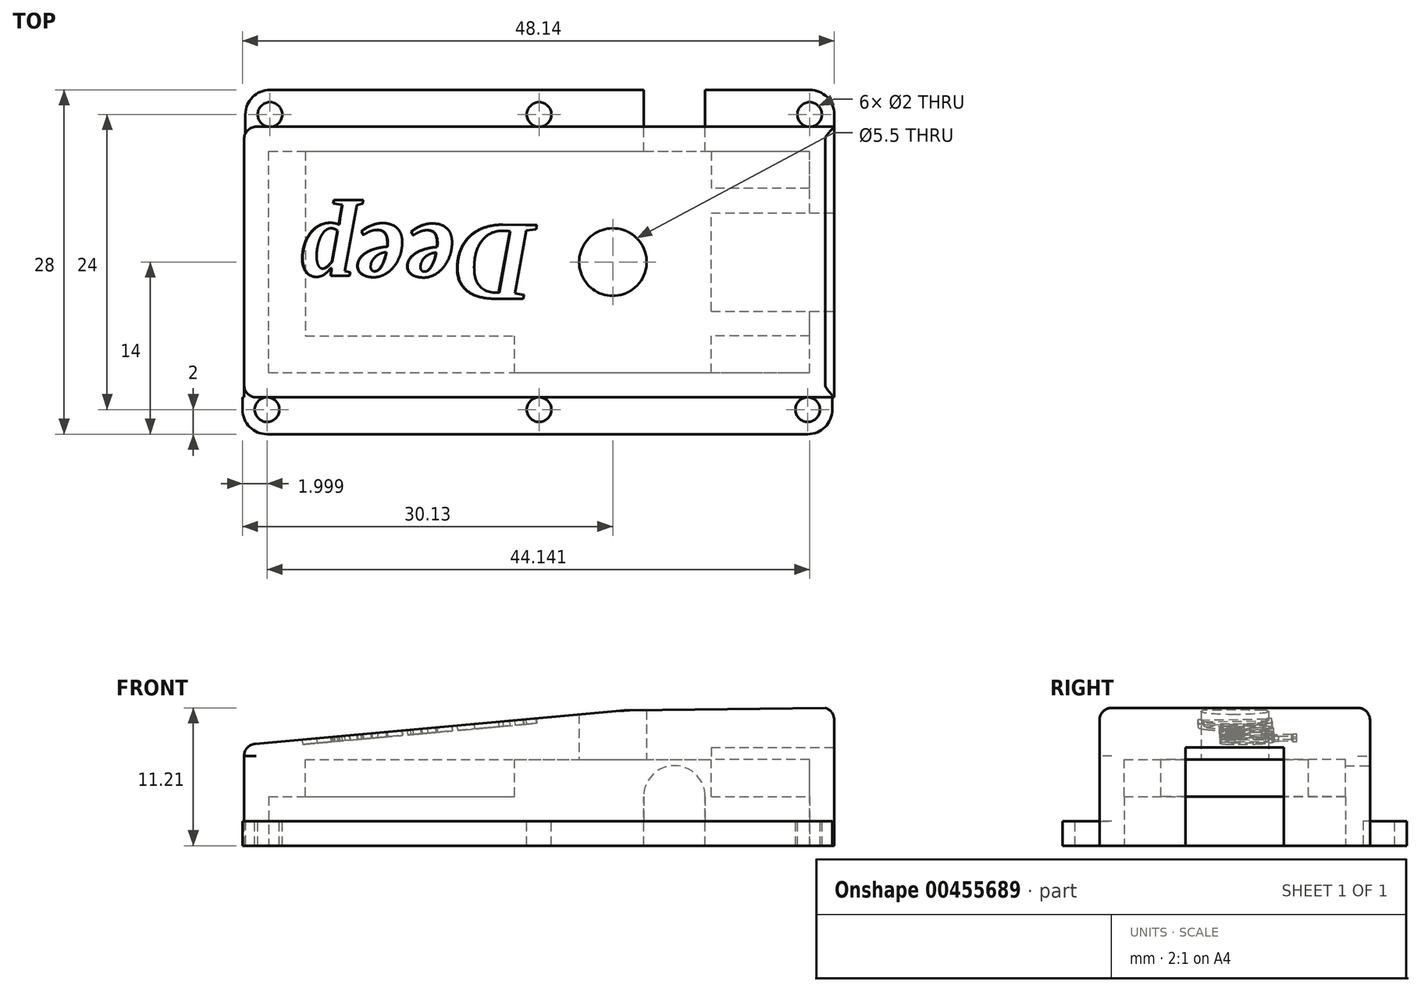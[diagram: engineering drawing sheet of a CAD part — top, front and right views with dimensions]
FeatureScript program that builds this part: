
annotation { "Feature Type Name" : "Feature", "Feature Type Description" : "" }
export const myFeature = defineFeature(function(context is Context, id is Id, definition is map)
    precondition{}
    {
        {
            var Q0;
            Q0=qCreatedBy(makeId("Front.planeOp"),FACE);
            var sketch = newSketch(context, id + "F0", { "sketchPlane" : qUnion([Q0])});
            skLineSegment(sketch, "E0", {"start": v(-24, 0) * mm, "end": v(-24, 7.34) * mm});
            skLineSegment(sketch, "E1", {"start": v(24, 0) * mm, "end": v(24, 10.25) * mm});
            skLineSegment(sketch, "E2", {"start": v(-24, 0) * mm, "end": v(24, 0) * mm});
            skPoint(sketch, "E3", {"position": v(7, 11) * mm});
            skPoint(sketch, "E4.visualSharp", {"position": v(-24, 8) * mm});
            skArc(sketch, "E4.filletArc", {"start": v(-23.4, 8.26) * mm, "mid": v(-23.83, 7.9) * mm, "end": v(-24, 7.34) * mm});
            skPoint(sketch, "E5.visualSharp", {"position": v(24, 9) * mm});
            skArc(sketch, "E5.filletArc", {"start": v(24, 10.25) * mm, "mid": v(23.8, 10.85) * mm, "end": v(23.27, 11.21) * mm});
            skLineSegment(sketch, "E6", {"start": v(-23.4, 8.26) * mm, "end": v(6.62, 10.97) * mm});
            skLineSegment(sketch, "E7", {"start": v(23.27, 11.21) * mm, "end": v(7.38, 11) * mm});
            skArc(sketch, "E8.filletArc", {"start": v(7.38, 11) * mm, "mid": v(7, 11) * mm, "end": v(6.62, 10.97) * mm});
            skSolve(sketch);
        }
        {
            var Q0;
            Q0=makeQuery(id+"F0.imprint","IMPRINT",FACE,{"disambiguationData":[TD([[makeQuery(id+"F0.imprint","IMPRINT",EDGE,{"derivedFrom":sQuery(id+"F0.wireOp",EDGE,"E0")}),-1.0]])]});
            extrude(context, id + "F1", {"entities" : qUnion([Q0]), "depth" : 22 * mm});
        }
        {
            var Q0;
            Q0=makeQuery(id+"F1.opExtrude","SWEPT_FACE",FACE,{"disambiguationData":[OSD([sQuery(id+"F0.wireOp",EDGE,"E2")])]});
            var sketch = newSketch(context, id + "F2", { "sketchPlane" : qUnion([Q0])});
            skLineSegment(sketch, "E9.bottom", {"start": v(-22, 20) * mm, "end": v(22, 20) * mm});
            skLineSegment(sketch, "E9.top", {"start": v(-22, 2) * mm, "end": v(22, 2) * mm});
            skLineSegment(sketch, "E9.left", {"start": v(-22, 20) * mm, "end": v(-22, 2) * mm});
            skLineSegment(sketch, "E9.right", {"start": v(22, 20) * mm, "end": v(22, 2) * mm});
            skSolve(sketch);
        }
        {
            var Q0;
            Q0=makeQuery(id+"F2.imprint","IMPRINT",FACE,{"disambiguationData":[TD([[makeQuery(id+"F2.imprint","IMPRINT",EDGE,{"derivedFrom":sQuery(id+"F2.wireOp",EDGE,"E9.bottom")}),-1.0]])]});
            extrude(context, id + "F3", {"entities" : qUnion([Q0]), "operationType" : NewBodyOperationType.REMOVE, "depth" : -7 * mm});
        }
        {
            var Q0;
            Q0=makeQuery(id+"F3.boolean.opBoolean","COPY",FACE,{"derivedFrom":makeQuery(id+"F3.opExtrude","CAP_FACE",FACE,{"disambiguationData":[OSD([sQuery(id+"F2.wireOp",EDGE,"E9.bottom"),sQuery(id+"F2.wireOp",EDGE,"E9.top"),sQuery(id+"F2.wireOp",EDGE,"E9.left"),sQuery(id+"F2.wireOp",EDGE,"E9.right")])],"isStart":false})});
            var sketch = newSketch(context, id + "F4", { "sketchPlane" : qUnion([Q0])});
            skLineSegment(sketch, "E10.bottom", {"start": v(14, 15) * mm, "end": v(22, 15) * mm});
            skLineSegment(sketch, "E10.top", {"start": v(14, 7) * mm, "end": v(22, 7) * mm});
            skLineSegment(sketch, "E10.left", {"start": v(14, 15) * mm, "end": v(14, 7) * mm});
            skLineSegment(sketch, "E10.right", {"start": v(22, 15) * mm, "end": v(22, 7) * mm});
            skSolve(sketch);
        }
        {
            var Q0;
            Q0=makeQuery(id+"F4.imprint","IMPRINT",FACE,{"disambiguationData":[TD([[makeQuery(id+"F4.imprint","IMPRINT",EDGE,{"derivedFrom":sQuery(id+"F4.wireOp",EDGE,"E10.bottom")}),-1.0]])]});
            extrude(context, id + "F5", {"entities" : qUnion([Q0]), "operationType" : NewBodyOperationType.REMOVE, "depth" : -1 * mm});
        }
        {
            var Q0;
            Q0=makeQuery(id+"F1.opExtrude","SWEPT_FACE",FACE,{"disambiguationData":[OSD([sQuery(id+"F0.wireOp",EDGE,"E1")])]});
            var sketch = newSketch(context, id + "F6", { "sketchPlane" : qUnion([Q0])});
            skLineSegment(sketch, "E11.bottom", {"start": v(-15, 0) * mm, "end": v(-7, 0) * mm});
            skLineSegment(sketch, "E11.top", {"start": v(-15, 8) * mm, "end": v(-7, 8) * mm});
            skLineSegment(sketch, "E11.left", {"start": v(-15, 0) * mm, "end": v(-15, 8) * mm});
            skLineSegment(sketch, "E11.right", {"start": v(-7, 0) * mm, "end": v(-7, 8) * mm});
            skSolve(sketch);
        }
        {
            var Q0;
            {var subQ0=sQuery(id+"F6.wireOp",EDGE,"E11.bottom");Q0=makeQuery(id+"F6.imprint","IMPRINT",FACE,{"disambiguationData":[TD([[makeQuery(id+"F6.imprint","IMPRINT",EDGE,{"derivedFrom":subQ0}),1.0]])]});}
            var Q1;
            {var subQ0=sQuery(id+"F6.wireOp",EDGE,"E11.top");Q1=makeQuery(id+"F6.imprint","IMPRINT",FACE,{"disambiguationData":[TD([[makeQuery(id+"F6.imprint","IMPRINT",EDGE,{"derivedFrom":subQ0}),-1.0]])]});}
            extrude(context, id + "F7", {"entities" : qUnion([Q0, Q1]), "operationType" : NewBodyOperationType.REMOVE, "oppositeDirection" : true, "depth" : 2 * mm});
        }
        {
            var Q0;
            Q0=makeQuery(id+"F3.boolean.opBoolean","COPY",FACE,{"derivedFrom":makeQuery(id+"F3.opExtrude","CAP_FACE",FACE,{"disambiguationData":[OSD([sQuery(id+"F2.wireOp",EDGE,"E9.bottom"),sQuery(id+"F2.wireOp",EDGE,"E9.top"),sQuery(id+"F2.wireOp",EDGE,"E9.left"),sQuery(id+"F2.wireOp",EDGE,"E9.right")])],"isStart":false})});
            var sketch = newSketch(context, id + "F8", { "sketchPlane" : qUnion([Q0])});
            skCircle(sketch, "E12", {"center": v(6, 11) * mm, "radius": 2.75 * mm});
            skSolve(sketch);
        }
        {
            var Q0;
            Q0=makeQuery(id+"F8.imprint","IMPRINT",FACE,{"disambiguationData":[TD([[makeQuery(id+"F8.imprint","IMPRINT",EDGE,{"derivedFrom":sQuery(id+"F8.wireOp",EDGE,"E12")}),1.0]])]});
            extrude(context, id + "F9", {"entities" : qUnion([Q0]), "operationType" : NewBodyOperationType.REMOVE, "oppositeDirection" : true, "depth" : 10 * mm});
        }
        {
            var Q0;
            Q0=makeQuery(id+"F3.boolean.opBoolean","COPY",FACE,{"derivedFrom":makeQuery(id+"F3.opExtrude","CAP_FACE",FACE,{"disambiguationData":[OSD([sQuery(id+"F2.wireOp",EDGE,"E9.bottom"),sQuery(id+"F2.wireOp",EDGE,"E9.top"),sQuery(id+"F2.wireOp",EDGE,"E9.left"),sQuery(id+"F2.wireOp",EDGE,"E9.right")])],"isStart":false})});
            var sketch = newSketch(context, id + "F10", { "sketchPlane" : qUnion([Q0])});
            skLineSegment(sketch, "E13.bottom", {"start": v(22, 2) * mm, "end": v(14, 2) * mm});
            skLineSegment(sketch, "E13.top", {"start": v(22, 5) * mm, "end": v(14, 5) * mm});
            skLineSegment(sketch, "E13.left", {"start": v(22, 2) * mm, "end": v(22, 5) * mm});
            skLineSegment(sketch, "E13.right", {"start": v(14, 2) * mm, "end": v(14, 5) * mm});
            skLineSegment(sketch, "E14.bottom", {"start": v(22, 20) * mm, "end": v(14, 20) * mm});
            skLineSegment(sketch, "E14.top", {"start": v(22, 17) * mm, "end": v(14, 17) * mm});
            skLineSegment(sketch, "E14.left", {"start": v(22, 20) * mm, "end": v(22, 17) * mm});
            skLineSegment(sketch, "E14.right", {"start": v(14, 20) * mm, "end": v(14, 17) * mm});
            skLineSegment(sketch, "E15.bottom", {"start": v(-22, 20) * mm, "end": v(-2, 20) * mm});
            skLineSegment(sketch, "E15.top", {"start": v(-22, 17) * mm, "end": v(-2, 17) * mm});
            skLineSegment(sketch, "E15.left", {"start": v(-22, 20) * mm, "end": v(-22, 17) * mm});
            skLineSegment(sketch, "E15.right", {"start": v(-2, 20) * mm, "end": v(-2, 17) * mm});
            skLineSegment(sketch, "E16.bottom", {"start": v(-22, 2) * mm, "end": v(-19, 2) * mm});
            skLineSegment(sketch, "E16.top", {"start": v(-22, 5) * mm, "end": v(-19, 5) * mm});
            skLineSegment(sketch, "E16.left", {"start": v(-22, 2) * mm, "end": v(-22, 5) * mm});
            skLineSegment(sketch, "E16.right", {"start": v(-19, 2) * mm, "end": v(-19, 5) * mm});
            skSolve(sketch);
        }
        {
            var Q0;
            Q0=makeQuery(id+"F10.imprint","IMPRINT",FACE,{"disambiguationData":[TD([[makeQuery(id+"F10.imprint","IMPRINT",EDGE,{"derivedFrom":sQuery(id+"F10.wireOp",EDGE,"E15.bottom")}),-1.0]])]});
            var Q1;
            Q1=makeQuery(id+"F10.imprint","IMPRINT",FACE,{"disambiguationData":[TD([[makeQuery(id+"F10.imprint","IMPRINT",EDGE,{"derivedFrom":sQuery(id+"F10.wireOp",EDGE,"E16.bottom")}),1.0]])]});
            var Q2;
            Q2=makeQuery(id+"F10.imprint","IMPRINT",FACE,{"disambiguationData":[TD([[makeQuery(id+"F10.imprint","IMPRINT",EDGE,{"derivedFrom":sQuery(id+"F10.wireOp",EDGE,"E13.bottom")}),1.0]])]});
            var Q3;
            Q3=makeQuery(id+"F10.imprint","IMPRINT",FACE,{"disambiguationData":[TD([[makeQuery(id+"F10.imprint","IMPRINT",EDGE,{"derivedFrom":sQuery(id+"F10.wireOp",EDGE,"E14.bottom")}),-1.0]])]});
            extrude(context, id + "F11", {"entities" : qUnion([Q0, Q1, Q2, Q3]), "operationType" : NewBodyOperationType.ADD, "depth" : 3 * mm});
        }
        {
            var Q0;
            Q0=makeQuery(id+"F1.opExtrude","CAP_FACE",FACE,{"disambiguationData":[OSD([sQuery(id+"F0.wireOp",EDGE,"E0"),sQuery(id+"F0.wireOp",EDGE,"E1"),sQuery(id+"F0.wireOp",EDGE,"E2"),sQuery(id+"F0.wireOp",EDGE,"Oknbtmik-333Q-qwfd-Srco-IpxuO3KOyoef"),sQuery(id+"F0.wireOp",EDGE,"E4.filletArc"),sQuery(id+"F0.wireOp",EDGE,"E5.filletArc")])],"isStart":true});
            var sketch = newSketch(context, id + "F12", { "sketchPlane" : qUnion([Q0])});
            skLineSegment(sketch, "E17.bottom", {"start": v(-24.01, 2) * mm, "end": v(23.9, 2) * mm});
            skLineSegment(sketch, "E17.top", {"start": v(-24.01, 0) * mm, "end": v(23.9, 0) * mm});
            skLineSegment(sketch, "E17.left", {"start": v(-24.01, 2) * mm, "end": v(-24.01, 0) * mm});
            skLineSegment(sketch, "E17.right", {"start": v(23.9, 2) * mm, "end": v(23.9, 0) * mm});
            skSolve(sketch);
        }
        {
            var Q0;
            Q0=makeQuery(id+"F12.imprint","IMPRINT",FACE,{"disambiguationData":[TD([[makeQuery(id+"F12.imprint","IMPRINT",EDGE,{"derivedFrom":sQuery(id+"F12.wireOp",EDGE,"E17.bottom")}),-1.0]])]});
            extrude(context, id + "F13", {"entities" : qUnion([Q0]), "operationType" : NewBodyOperationType.ADD, "depth" : 3 * mm});
        }
        {
            var Q0;
            Q0=makeQuery(id+"F1.opExtrude","CAP_FACE",FACE,{"disambiguationData":[OSD([sQuery(id+"F0.wireOp",EDGE,"E0"),sQuery(id+"F0.wireOp",EDGE,"E1"),sQuery(id+"F0.wireOp",EDGE,"E2"),sQuery(id+"F0.wireOp",EDGE,"Oknbtmik-333Q-qwfd-Srco-IpxuO3KOyoef"),sQuery(id+"F0.wireOp",EDGE,"E4.filletArc"),sQuery(id+"F0.wireOp",EDGE,"E5.filletArc")])],"isStart":false});
            var sketch = newSketch(context, id + "F14", { "sketchPlane" : qUnion([Q0])});
            skLineSegment(sketch, "E18.bottom", {"start": v(-24.13, 2) * mm, "end": v(23.85, 2) * mm});
            skLineSegment(sketch, "E18.top", {"start": v(-24.13, 0) * mm, "end": v(23.85, 0) * mm});
            skLineSegment(sketch, "E18.left", {"start": v(-24.13, 2) * mm, "end": v(-24.13, 0) * mm});
            skLineSegment(sketch, "E18.right", {"start": v(23.85, 2) * mm, "end": v(23.85, 0) * mm});
            skSolve(sketch);
        }
        {
            var Q0;
            Q0=makeQuery(id+"F14.imprint","IMPRINT",FACE,{"disambiguationData":[TD([[makeQuery(id+"F14.imprint","IMPRINT",EDGE,{"derivedFrom":sQuery(id+"F14.wireOp",EDGE,"E18.bottom")}),-1.0]])]});
            extrude(context, id + "F15", {"entities" : qUnion([Q0]), "operationType" : NewBodyOperationType.ADD, "depth" : 3 * mm});
        }
        {
            var Q0;
            Q0=makeQuery(id+"F13.opExtrude","CAP_EDGE",EDGE,{"disambiguationData":[OSD([sQuery(id+"F12.wireOp",EDGE,"E17.right")])],"isStart":false});
            fillet(context, id + "F16", {"entities" : qUnion([Q0]), "radius" : 2 * mm, "tangentPropagation" : true, "allowEdgeOverflow" : false});
        }
        {
            var Q0;
            Q0=makeQuery(id+"F13.opExtrude","CAP_EDGE",EDGE,{"disambiguationData":[OSD([sQuery(id+"F12.wireOp",EDGE,"E17.left")])],"isStart":false});
            var Q1;
            Q1=makeQuery(id+"F15.opExtrude","CAP_EDGE",EDGE,{"disambiguationData":[OSD([sQuery(id+"F14.wireOp",EDGE,"E18.right")])],"isStart":false});
            var Q2;
            Q2=makeQuery(id+"F15.opExtrude","CAP_EDGE",EDGE,{"disambiguationData":[OSD([sQuery(id+"F14.wireOp",EDGE,"E18.left")])],"isStart":false});
            fillet(context, id + "F17", {"entities" : qUnion([Q0, Q1, Q2]), "radius" : 2 * mm, "tangentPropagation" : true, "allowEdgeOverflow" : false});
        }
        {
            var Q0;
            Q0=makeQuery(id+"F13.opExtrude","SWEPT_FACE",FACE,{"disambiguationData":[OSD([sQuery(id+"F12.wireOp",EDGE,"E17.bottom")])]});
            var sketch = newSketch(context, id + "F18", { "sketchPlane" : qUnion([Q0])});
            skCircle(sketch, "E19", {"center": v(0, 1) * mm, "radius": 1 * mm});
            skCircle(sketch, "E20", {"center": v(22.01, 1) * mm, "radius": 1 * mm});
            skCircle(sketch, "E21", {"center": v(-21.9, 1) * mm, "radius": 1 * mm});
            skCircle(sketch, "E22", {"center": v(0, -23) * mm, "radius": 1 * mm});
            skCircle(sketch, "E23", {"center": v(-22.13, -23) * mm, "radius": 1 * mm});
            skCircle(sketch, "E24", {"center": v(21.85, -23) * mm, "radius": 1 * mm});
            skSolve(sketch);
        }
        {
            var Q0;
            Q0=makeQuery(id+"F18.imprint","IMPRINT",FACE,{"disambiguationData":[TD([[makeQuery(id+"F18.imprint","IMPRINT",EDGE,{"derivedFrom":sQuery(id+"F18.wireOp",EDGE,"E21")}),1.0]])]});
            var Q1;
            Q1=makeQuery(id+"F18.imprint","IMPRINT",FACE,{"disambiguationData":[TD([[makeQuery(id+"F18.imprint","IMPRINT",EDGE,{"derivedFrom":sQuery(id+"F18.wireOp",EDGE,"E19")}),1.0]])]});
            var Q2;
            Q2=makeQuery(id+"F18.imprint","IMPRINT",FACE,{"disambiguationData":[TD([[makeQuery(id+"F18.imprint","IMPRINT",EDGE,{"derivedFrom":sQuery(id+"F18.wireOp",EDGE,"E20")}),1.0]])]});
            var Q3;
            Q3=makeQuery(id+"F18.imprint","IMPRINT",FACE,{"disambiguationData":[TD([[makeQuery(id+"F18.imprint","IMPRINT",EDGE,{"derivedFrom":sQuery(id+"F18.wireOp",EDGE,"E23")}),1.0]])]});
            var Q4;
            Q4=makeQuery(id+"F18.imprint","IMPRINT",FACE,{"disambiguationData":[TD([[makeQuery(id+"F18.imprint","IMPRINT",EDGE,{"derivedFrom":sQuery(id+"F18.wireOp",EDGE,"E22")}),1.0]])]});
            var Q5;
            Q5=makeQuery(id+"F18.imprint","IMPRINT",FACE,{"disambiguationData":[TD([[makeQuery(id+"F18.imprint","IMPRINT",EDGE,{"derivedFrom":sQuery(id+"F18.wireOp",EDGE,"E24")}),1.0]])]});
            extrude(context, id + "F19", {"entities" : qUnion([Q0, Q1, Q2, Q3, Q4, Q5]), "operationType" : NewBodyOperationType.REMOVE, "oppositeDirection" : true, "depth" : 2 * mm});
        }
        {
            var Q0;
            {var subQ0=sQuery(id+"F0.wireOp",EDGE,"E0");Q0=makeQuery(id+"F15.boolean.opBoolean","SPLIT",EDGE,{"disambiguationData":[topologyDisambiguationEdgeConnected([makeQuery(id+"F1.opExtrude","CAP_FACE",FACE,{"disambiguationData":[OSD([subQ0,sQuery(id+"F0.wireOp",EDGE,"E1"),sQuery(id+"F0.wireOp",EDGE,"E2"),sQuery(id+"F0.wireOp",EDGE,"E4.filletArc"),sQuery(id+"F0.wireOp",EDGE,"6WC63ifF-hcEu-kARe-1SZb-fn5sgA7jzdy6")])],"isStart":false})])],"derivedFrom":makeQuery(id+"F1.opExtrude","CAP_EDGE",EDGE,{"disambiguationData":[OSD([subQ0])],"isStart":false})});}
            fillet(context, id + "F20", {"entities" : qUnion([Q0]), "radius" : 1 * mm, "tangentPropagation" : true, "allowEdgeOverflow" : false});
        }
        {
            var Q0;
            Q0=makeQuery(id+"F1.opExtrude","CAP_EDGE",EDGE,{"disambiguationData":[OSD([sQuery(id+"F0.wireOp",EDGE,"E0")])],"isStart":true});
            fillet(context, id + "F21", {"entities" : qUnion([Q0]), "radius" : 1 * mm, "tangentPropagation" : true, "allowEdgeOverflow" : false});
        }
        {
            var Q0;
            Q0=makeQuery(id+"F13.opExtrude","CAP_FACE",FACE,{"disambiguationData":[OSD([sQuery(id+"F12.wireOp",EDGE,"E17.bottom"),sQuery(id+"F12.wireOp",EDGE,"E17.top"),sQuery(id+"F12.wireOp",EDGE,"E17.left"),sQuery(id+"F12.wireOp",EDGE,"E17.right")])],"isStart":false});
            var sketch = newSketch(context, id + "F22", { "sketchPlane" : qUnion([Q0])});
            skLineSegment(sketch, "E25.bottom", {"start": v(-13.51, 0) * mm, "end": v(-8.51, 0) * mm});
            skLineSegment(sketch, "E25.top", {"start": v(-11.01, 6.5) * mm, "end": v(-11.01, 6.5) * mm});
            skLineSegment(sketch, "E25.left", {"start": v(-13.51, 0) * mm, "end": v(-13.51, 4) * mm});
            skLineSegment(sketch, "E25.right", {"start": v(-8.51, 0) * mm, "end": v(-8.51, 4) * mm});
            skPoint(sketch, "E26.visualSharp", {"position": v(-13.51, 6.5) * mm});
            skArc(sketch, "E26.filletArc", {"start": v(-11.01, 6.5) * mm, "mid": v(-12.78, 5.77) * mm, "end": v(-13.51, 4) * mm});
            skPoint(sketch, "E27.visualSharp", {"position": v(-8.51, 6.5) * mm});
            skArc(sketch, "E27.filletArc", {"start": v(-8.51, 4) * mm, "mid": v(-9.24, 5.77) * mm, "end": v(-11.01, 6.5) * mm});
            skSolve(sketch);
        }
        {
            var Q0;
            {var subQ0=sQuery(id+"F22.wireOp",EDGE,"E25.bottom");Q0=makeQuery(id+"F22.imprint","IMPRINT",FACE,{"disambiguationData":[TD([[makeQuery(id+"F22.imprint","IMPRINT",EDGE,{"derivedFrom":subQ0}),1.0]])]});}
            var Q1;
            {var subQ1=sQuery(id+"F22.wireOp",EDGE,"E26.filletArc");Q1=makeQuery(id+"F22.imprint","IMPRINT",FACE,{"disambiguationData":[TD([[makeQuery(id+"F22.imprint","IMPRINT",EDGE,{"derivedFrom":subQ1}),1.0]])]});}
            extrude(context, id + "F23", {"entities" : qUnion([Q0, Q1]), "operationType" : NewBodyOperationType.REMOVE, "oppositeDirection" : true, "depth" : 6 * mm});
        }
        {
            var Q0;
            Q0=makeQuery(id+"F3.boolean.opBoolean","COPY",FACE,{"derivedFrom":makeQuery(id+"F3.opExtrude","CAP_FACE",FACE,{"disambiguationData":[OSD([sQuery(id+"F2.wireOp",EDGE,"E9.bottom"),sQuery(id+"F2.wireOp",EDGE,"E9.top"),sQuery(id+"F2.wireOp",EDGE,"E9.left"),sQuery(id+"F2.wireOp",EDGE,"E9.right")])],"isStart":false})});
            var sketch = newSketch(context, id + "F24", { "sketchPlane" : qUnion([Q0])});
            skLineSegment(sketch, "E28.bottom", {"start": v(-22, 17) * mm, "end": v(-19, 17) * mm});
            skLineSegment(sketch, "E28.top", {"start": v(-22, 5) * mm, "end": v(-19, 5) * mm});
            skLineSegment(sketch, "E28.left", {"start": v(-22, 17) * mm, "end": v(-22, 5) * mm});
            skLineSegment(sketch, "E28.right", {"start": v(-19, 17) * mm, "end": v(-19, 5) * mm});
            skSolve(sketch);
        }
        {
            var Q0;
            Q0=makeQuery(id+"F24.imprint","IMPRINT",FACE,{"disambiguationData":[TD([[makeQuery(id+"F24.imprint","IMPRINT",EDGE,{"derivedFrom":sQuery(id+"F24.wireOp",EDGE,"E28.bottom")}),-1.0]])]});
            extrude(context, id + "F25", {"entities" : qUnion([Q0]), "operationType" : NewBodyOperationType.ADD, "depth" : 3 * mm});
        }
        {
            var Q0;
            Q0=makeQuery(id+"F1.opExtrude","CAP_EDGE",EDGE,{"disambiguationData":[OSD([sQuery(id+"F0.wireOp",EDGE,"E7")])],"isStart":true});
            var Q1;
            Q1=makeQuery(id+"F1.opExtrude","CAP_EDGE",EDGE,{"disambiguationData":[OSD([sQuery(id+"F0.wireOp",EDGE,"E6")])],"isStart":false});
            fillet(context, id + "F26", {"entities" : qUnion([Q0, Q1]), "radius" : 1 * mm, "tangentPropagation" : true, "allowEdgeOverflow" : false});
        }
        {
            var Q0;
            Q0=makeQuery(id+"F1.opExtrude","SWEPT_FACE",FACE,{"disambiguationData":[OSD([sQuery(id+"F0.wireOp",EDGE,"E6")])]});
            var sketch = newSketch(context, id + "F27", { "sketchPlane" : qUnion([Q0])});
            skText(sketch, "E29", { "text": "Deep", "fontName": "Tinos-BoldItalic.ttf"});
            const initialGuessF27  = {"E29": [0.00066, -0.008, -0.99998, 0.00612, 0.0066]};
            skSetInitialGuess(sketch, initialGuessF27);
            skSolve(sketch);
        }
        {
            var Q0;
            Q0 = qSketchRegion(id + "F27", true);
            extrude(context, id + "F28", {"entities" : qUnion([Q0]), "operationType" : NewBodyOperationType.REMOVE, "oppositeDirection" : true, "depth" : .4 * mm});
        }
    });
